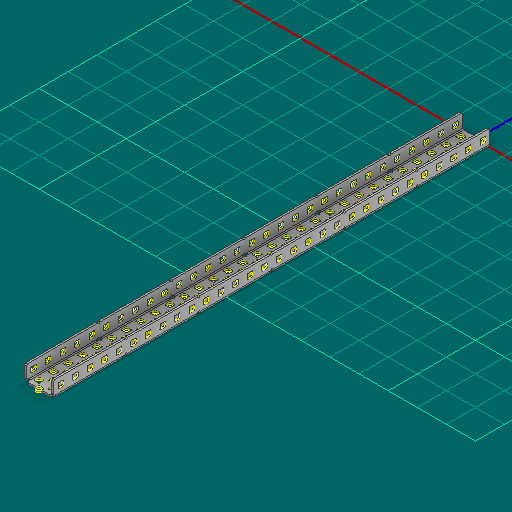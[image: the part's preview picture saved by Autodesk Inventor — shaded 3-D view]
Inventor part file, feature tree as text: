
AUTODESK INVENTOR PART (.ipt)
format: ipt  version: 2025 (Build 290162000, 162)  size: 2,446,848 bytes
history: native  units: in
note: dims shown in document units (in); Inventor stores cm internally (conversion verified against a paired STEP export)
features: other x306, sketch x5, sheet_metal_op x1
ambient origin geometry x8: Origin, YZ Plane, XZ Plane, XY Plane, X Axis, Y Axis, Z Axis, Center Point
bodies: Solid1 (feature_tree)
feature tree (312):
  other  "Alu C 1x2x1x30.ipt"
  other  "Solid1::Alu C 1x2x1x30.ipt"
  other  "TaggingFeature1"
  sketch  "Sketch1"  dims[d0=0.3937in]
  sketch  "Sketch2"  dims[d1=0.0625in]
  sketch  "Sketch3"
  other  "Flange Pattern Sketch"
  sketch  "Sketch9"
  sheet_metal_op  "Body Pattern Sketch"
  other  "Arc Length"
  sketch  "Sketch14"
  other  "Flange Pattern Plane"
  other  "Srf1"
  other  "Srf2"
  other  "Srf3"
  other  "Srf4"
  other  "Srf5"
  other  "Srf6"
  other  "Srf7"
  other  "Srf8"
  other  "Srf9"
  other  "Srf10"
  other  "Srf11"
  other  "Srf12"
  other  "Srf13"
  other  "Srf14"
  other  "Srf15"
  other  "Srf16"
  other  "Srf17"
  other  "Srf18"
  other  "Srf19"
  other  "Srf20"
  other  "Srf21"
  other  "Srf22"
  other  "Srf23"
  other  "Srf24"
  other  "Srf25"
  other  "Srf26"
  other  "Srf27"
  other  "Srf28"
  other  "Srf29"
  other  "Srf30"
  other  "Srf31"
  other  "Srf32"
  other  "Srf33"
  other  "Srf34"
  other  "Srf35"
  other  "Srf36"
  other  "Srf37"
  other  "Srf38"
  other  "Srf39"
  other  "Srf40"
  other  "Srf41"
  other  "Srf42"
  other  "Srf43"
  other  "Srf44"
  other  "Srf45"
  other  "Srf46"
  other  "Srf47"
  other  "Srf48"
  other  "Srf49"
  other  "Srf50"
  other  "Srf51"
  other  "Srf52"
  other  "Srf53"
  other  "Srf54"
  other  "Srf55"
  other  "Srf56"
  other  "Srf57"
  other  "Srf58"
  other  "Srf59"
  other  "Srf60"
  other  "Srf61"
  other  "Srf62"
  other  "Srf63"
  other  "Srf64"
  other  "Srf65"
  other  "Srf66"
  other  "Srf67"
  other  "Srf68"
  other  "Srf69"
  other  "Srf70"
  other  "Srf71"
  other  "Srf72"
  other  "Srf73"
  other  "Srf74"
  other  "Srf75"
  other  "Srf76"
  other  "Srf77"
  other  "Srf78"
  other  "Srf79"
  other  "Srf80"
  other  "Srf81"
  other  "Srf82"
  other  "Srf83"
  other  "Srf84"
  other  "Srf85"
  other  "Srf86"
  other  "Srf87"
  other  "Srf88"
  other  "Srf89"
  other  "Srf90"
  other  "Srf91"
  other  "Srf92"
  other  "Srf93"
  other  "Srf94"
  other  "Srf95"
  other  "Srf96"
  other  "Srf97"
  other  "Srf98"
  other  "Srf99"
  other  "Srf100"
  other  "Srf101"
  other  "Srf102"
  other  "Srf103"
  other  "Srf104"
  other  "Srf105"
  other  "Srf106"
  other  "Srf107"
  other  "Srf108"
  other  "Srf109"
  other  "Srf110"
  other  "Srf111"
  other  "Srf112"
  other  "Srf113"
  other  "Srf114"
  other  "Srf115"
  other  "Srf116"
  other  "Srf117"
  other  "Srf118"
  other  "Srf119"
  other  "Srf120"
  other  "Srf121"
  other  "Srf122"
  other  "Srf123"
  other  "Srf124"
  other  "Srf125"
  other  "Srf126"
  other  "Srf127"
  other  "Srf128"
  other  "Srf129"
  other  "Srf130"
  other  "Srf131"
  other  "Srf132"
  other  "Srf133"
  other  "Srf134"
  other  "Srf135"
  other  "Srf136"
  other  "Srf137"
  other  "Srf138"
  other  "Srf139"
  other  "Srf140"
  other  "Srf141"
  other  "Srf142"
  other  "Srf143"
  other  "Srf144"
  other  "Srf145"
  other  "Srf146"
  other  "Srf147"
  other  "Srf148"
  other  "Srf149"
  other  "Srf150"
  other  "Srf1::Derived"
  other  "Srf2::Derived"
  other  "Srf823::Derived"
  other  "Srf824::Derived"
  other  "Srf825::Derived"
  other  "Srf826::Derived"
  other  "Srf827::Derived"
  other  "Srf828::Derived"
  other  "Srf829::Derived"
  other  "Srf922::Derived"
  other  "Srf923::Derived"
  other  "Srf924::Derived"
  other  "Srf925::Derived"
  other  "Srf926::Derived"
  other  "Srf1143::Derived"
  other  "Srf1144::Derived"
  other  "Srf1145::Derived"
  other  "Srf1146::Derived"
  other  "Srf1147::Derived"
  other  "Srf1148::Derived"
  other  "Srf1149::Derived"
  other  "Srf1150::Derived"
  other  "Srf1151::Derived"
  other  "Srf1152::Derived"
  other  "Srf1153::Derived"
  other  "Srf1154::Derived"
  other  "Srf1155::Derived"
  other  "Srf1156::Derived"
  other  "Srf1157::Derived"
  other  "Srf1158::Derived"
  other  "Srf1159::Derived"
  other  "Srf1160::Derived"
  other  "Srf1161::Derived"
  other  "Srf1162::Derived"
  other  "Srf1163::Derived"
  other  "Srf1164::Derived"
  other  "Srf1165::Derived"
  other  "Srf1166::Derived"
  other  "Srf1167::Derived"
  other  "Srf1168::Derived"
  other  "Srf1169::Derived"
  other  "Srf1170::Derived"
  other  "Srf1171::Derived"
  other  "Srf1172::Derived"
  other  "Srf1173::Derived"
  other  "Srf1174::Derived"
  other  "Srf1175::Derived"
  other  "Srf1176::Derived"
  other  "Srf1177::Derived"
  other  "Srf1178::Derived"
  other  "Srf1179::Derived"
  other  "Srf1180::Derived"
  other  "Srf1181::Derived"
  other  "Srf1182::Derived"
  other  "Srf1183::Derived"
  other  "Srf1184::Derived"
  other  "Srf1185::Derived"
  other  "Srf1186::Derived"
  other  "Srf1187::Derived"
  other  "Srf1188::Derived"
  other  "Srf91::Derived"
  other  "Srf92::Derived"
  other  "Srf856::Derived"
  other  "Srf857::Derived"
  other  "Srf858::Derived"
  other  "Srf859::Derived"
  other  "Srf860::Derived"
  other  "Srf861::Derived"
  other  "Srf862::Derived"
  other  "Srf959::Derived"
  other  "Srf960::Derived"
  other  "Srf961::Derived"
  other  "Srf962::Derived"
  other  "Srf963::Derived"
  other  "Srf1199::Derived"
  other  "Srf1200::Derived"
  other  "Srf1201::Derived"
  other  "Srf1202::Derived"
  other  "Srf1203::Derived"
  other  "Srf1204::Derived"
  other  "Srf1205::Derived"
  other  "Srf1206::Derived"
  other  "Srf1207::Derived"
  other  "Srf1208::Derived"
  other  "Srf1209::Derived"
  other  "Srf1210::Derived"
  other  "Srf1211::Derived"
  other  "Srf1212::Derived"
  other  "Srf1213::Derived"
  other  "Srf1214::Derived"
  other  "Srf1215::Derived"
  other  "Srf1216::Derived"
  other  "Srf1217::Derived"
  other  "Srf1218::Derived"
  other  "Srf1219::Derived"
  other  "Srf1220::Derived"
  other  "Srf1221::Derived"
  other  "Srf1222::Derived"
  other  "Srf1223::Derived"
  other  "Srf1224::Derived"
  other  "Srf1225::Derived"
  other  "Srf1226::Derived"
  other  "Srf1227::Derived"
  other  "Srf1228::Derived"
  other  "Srf1229::Derived"
  other  "Srf1230::Derived"
  other  "Srf1231::Derived"
  other  "Srf1232::Derived"
  other  "Srf1233::Derived"
  other  "Srf1234::Derived"
  other  "Srf1235::Derived"
  other  "Srf1236::Derived"
  other  "Srf1237::Derived"
  other  "Srf1238::Derived"
  other  "Srf1239::Derived"
  other  "Srf1240::Derived"
  other  "Srf1241::Derived"
  other  "Srf1242::Derived"
  other  "Srf1243::Derived"
  other  "Srf1244::Derived"
  other  "Srf786::Derived"
  other  "Srf889::Derived"
  other  "Srf890::Derived"
  other  "Srf891::Derived"
  other  "Srf892::Derived"
  other  "Srf893::Derived"
  other  "Srf894::Derived"
  other  "Srf895::Derived"
  other  "Srf896::Derived"
  other  "Srf996::Derived"
  other  "Srf997::Derived"
  other  "Srf998::Derived"
  other  "Srf999::Derived"
  other  "Srf1000::Derived"
  other  "Srf1255::Derived"
  other  "Srf1256::Derived"
  other  "Srf1257::Derived"
  other  "Srf1258::Derived"
  other  "Srf1259::Derived"
  other  "Srf1260::Derived"
  other  "Srf1261::Derived"
  other  "Srf1262::Derived"
  other  "Srf1263::Derived"
  other  "Srf1264::Derived"
  other  "Srf1265::Derived"
  other  "Srf1266::Derived"
  other  "Srf1267::Derived"
  other  "Srf1268::Derived"
  other  "Srf1269::Derived"
  other  "Srf1270::Derived"
